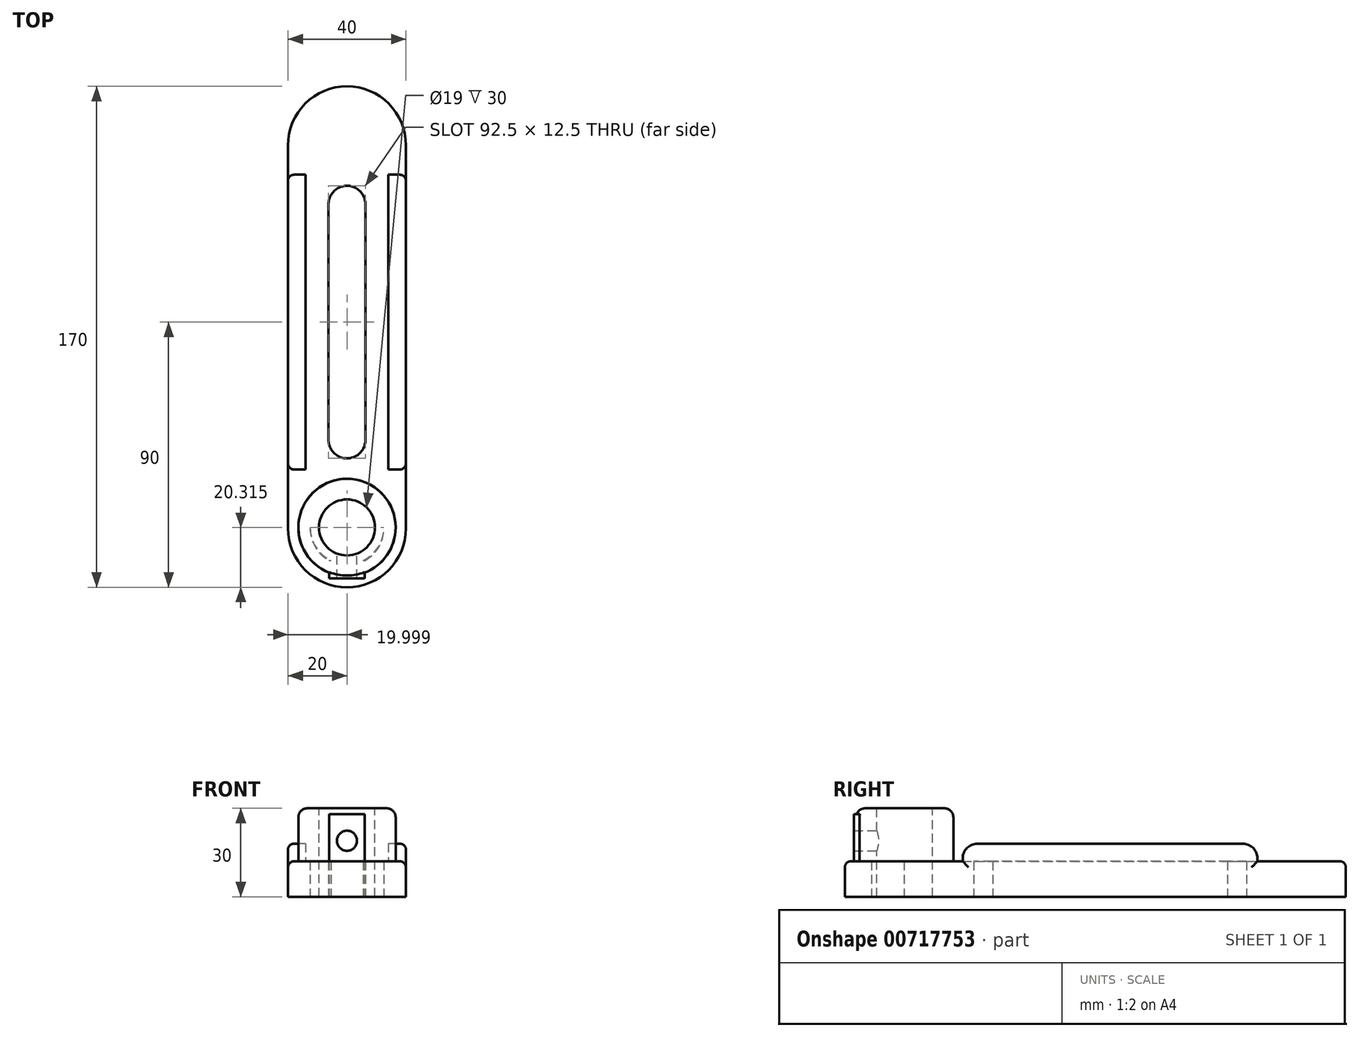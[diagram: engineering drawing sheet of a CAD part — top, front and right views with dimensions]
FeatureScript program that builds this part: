
annotation { "Feature Type Name" : "Feature", "Feature Type Description" : "" }
export const myFeature = defineFeature(function(context is Context, id is Id, definition is map)
    precondition{}
    {
        {
            var Q0;
            Q0=qCreatedBy(makeId("Top.planeOp"),FACE);
            var sketch = newSketch(context, id + "F0", { "sketchPlane" : qUnion([Q0])});
            skLineSegment(sketch, "E0.top", {"start": v(20, 80) * mm, "end": v(-20, 80) * mm});
            skLineSegment(sketch, "E0.left", {"start": v(20, -70) * mm, "end": v(20, 80) * mm});
            skLineSegment(sketch, "E0.right", {"start": v(-20, -70) * mm, "end": v(-20, 80) * mm});
            skPoint(sketch, "E0.middle", {"position": v(0, 0) * mm});
            skLineSegment(sketch, "E1", {"start": v(0, 0) * mm, "end": v(0, 40) * mm, "construction": true});
            skLineSegment(sketch, "E2", {"start": v(0, 40) * mm, "end": v(0, -40) * mm, "construction": true});
            skArc(sketch, "E3", {"start": v(-6.25, -40) * mm, "mid": v(0.07, -46.25) * mm, "end": v(6.25, -39.85) * mm});
            skArc(sketch, "E4", {"start": v(6.25, 39.85) * mm, "mid": v(0.07, 46.25) * mm, "end": v(-6.25, 40) * mm});
            skLineSegment(sketch, "E5", {"start": v(-6.25, 40) * mm, "end": v(-6.25, -40) * mm});
            skLineSegment(sketch, "E6", {"start": v(6.25, 40.15) * mm, "end": v(6.25, -40.15) * mm});
            skLineSegment(sketch, "E7", {"start": v(0, -90) * mm, "end": v(0, -70) * mm, "construction": true});
            skLineSegment(sketch, "E8", {"start": v(0, -70) * mm, "end": v(62.72, -70) * mm, "construction": true});
            skCircle(sketch, "E9", {"center": v(0, -70) * mm, "radius": 12.5 * mm});
            skArc(sketch, "E10", {"start": v(-20, -70) * mm, "mid": v(0, -90) * mm, "end": v(20, -70) * mm});
            skSolve(sketch);
        }
        {
            var Q0;
            Q0=makeQuery(id+"F0.imprint","IMPRINT",FACE,{"disambiguationData":[TD([[makeQuery(id+"F0.imprint","IMPRINT",EDGE,{"derivedFrom":sQuery(id+"F0.wireOp",EDGE,"E0.top")}),1.0]])]});
            extrude(context, id + "F1", {"entities" : qUnion([Q0]), "depth" : 12 * mm});
        }
        {
            var Q0;
            Q0=qCreatedBy(makeId("Top.planeOp"),FACE);
            var sketch = newSketch(context, id + "F2", { "sketchPlane" : qUnion([Q0])});
            skCircle(sketch, "E11", {"center": v(0, -69.69) * mm, "radius": 12.5 * mm});
            skCircle(sketch, "E12", {"center": v(0, -69.69) * mm, "radius": 16.5 * mm});
            skCircle(sketch, "E13", {"center": v(0, -69.69) * mm, "radius": 9.5 * mm});
            skSolve(sketch);
        }
        {
            var Q0;
            Q0=makeQuery(id+"F2.imprint","IMPRINT",FACE,{"disambiguationData":[TD([[makeQuery(id+"F2.imprint","IMPRINT",EDGE,{"derivedFrom":sQuery(id+"F2.wireOp",EDGE,"E11")}),-1.0]])]});
            var Q1;
            Q1=makeQuery(id+"F2.imprint","IMPRINT",FACE,{"disambiguationData":[TD([[makeQuery(id+"F2.imprint","IMPRINT",EDGE,{"derivedFrom":sQuery(id+"F2.wireOp",EDGE,"E11")}),1.0]])]});
            extrude(context, id + "F3", {"entities" : qUnion([Q0, Q1]), "operationType" : NewBodyOperationType.ADD, "depth" : 30 * mm, "hasSecondDirection" : true, "secondDirectionOppositeDirection" : false, "secondDirectionDepth" : 12 * mm});
        }
        {
            var Q0;
            Q0=makeQuery(id+"F2.imprint","IMPRINT",FACE,{"disambiguationData":[TD([[makeQuery(id+"F2.imprint","IMPRINT",EDGE,{"derivedFrom":sQuery(id+"F2.wireOp",EDGE,"E13")}),1.0]])]});
            var Q1;
            Q1=makeQuery(id+"F2.imprint","IMPRINT",FACE,{"disambiguationData":[TD([[makeQuery(id+"F2.imprint","IMPRINT",EDGE,{"derivedFrom":sQuery(id+"F2.wireOp",EDGE,"E11")}),1.0]])]});
            extrude(context, id + "F4", {"entities" : qUnion([Q0, Q1]), "operationType" : NewBodyOperationType.ADD, "depth" : 30 * mm});
        }
        {
            var Q0;
            Q0=qCreatedBy(makeId("Top.planeOp"),FACE);
            var sketch = newSketch(context, id + "F5", { "sketchPlane" : qUnion([Q0])});
            skCircle(sketch, "E14", {"center": v(0, -69.69) * mm, "radius": 9.5 * mm});
            skSolve(sketch);
        }
        {
            var Q0;
            Q0=qSketchRegion(id+"F5",true);
            extrude(context, id + "F6", {"entities" : qUnion([Q0]), "operationType" : NewBodyOperationType.REMOVE, "oppositeDirection" : true, "depth" : 25 * mm, "hasSecondDirection" : true, "secondDirectionOppositeDirection" : false, "secondDirectionDepth" : 100 * mm});
        }
        {
            var Q0;
            Q0=makeQuery(id+"F3.opExtrude","CAP_EDGE",EDGE,{"disambiguationData":[OSD([sQuery(id+"F2.wireOp",EDGE,"E12")])],"isStart":false});
            var Q1;
            Q1=makeQuery(id+"F3.opExtrude","CAP_EDGE",EDGE,{"disambiguationData":[OSD([sQuery(id+"F2.wireOp",EDGE,"E12")])],"isStart":true});
            fillet(context, id + "F7", {"entities" : qUnion([Q0, Q1]), "radius" : 3 * mm, "tangentPropagation" : true, "allowEdgeOverflow" : false});
        }
        {
            var Q0;
            Q0=qCreatedBy(makeId("Front.planeOp"),FACE);
            var sketch = newSketch(context, id + "F8", { "sketchPlane" : qUnion([Q0])});
            skLineSegment(sketch, "E15", {"start": v(14, 0) * mm, "end": v(20, 0) * mm, "construction": true});
            skLineSegment(sketch, "E16", {"start": v(20, 0) * mm, "end": v(20, 18) * mm});
            skLineSegment(sketch, "E17", {"start": v(20, 18) * mm, "end": v(14, 18) * mm});
            skLineSegment(sketch, "E18", {"start": v(14, 18) * mm, "end": v(14, 12) * mm});
            skLineSegment(sketch, "E19", {"start": v(-14, 12) * mm, "end": v(-14, 18) * mm});
            skLineSegment(sketch, "E20", {"start": v(-14, 18) * mm, "end": v(-20, 18) * mm});
            skLineSegment(sketch, "E21", {"start": v(-20, 18) * mm, "end": v(-20, 0) * mm});
            skLineSegment(sketch, "E22", {"start": v(-20, 0) * mm, "end": v(-14, 0) * mm});
            skLineSegment(sketch, "E23", {"start": v(-14, 12) * mm, "end": v(-14, 0) * mm});
            skLineSegment(sketch, "E24", {"start": v(14, 12) * mm, "end": v(14, 0) * mm});
            skLineSegment(sketch, "E25.trimOffspring", {"start": v(0, 0) * mm, "end": v(20, 0) * mm});
            skSolve(sketch);
        }
        {
            var Q0;
            Q0=qSketchRegion(id+"F8",true);
            extrude(context, id + "F9", {"entities" : qUnion([Q0]), "operationType" : NewBodyOperationType.ADD, "depth" : 50 * mm, "hasSecondDirection" : true, "secondDirectionOppositeDirection" : true, "secondDirectionDepth" : 50 * mm});
        }
        {
            var Q0;
            Q0=makeQuery(id+"F9.opExtrude","CAP_EDGE",EDGE,{"disambiguationData":[OSD([sQuery(id+"F8.wireOp",EDGE,"E17")])],"isStart":true});
            var Q1;
            Q1=makeQuery(id+"F9.opExtrude","CAP_EDGE",EDGE,{"disambiguationData":[OSD([sQuery(id+"F8.wireOp",EDGE,"E20")])],"isStart":true});
            var Q2;
            Q2=makeQuery(id+"F9.opExtrude","CAP_EDGE",EDGE,{"disambiguationData":[OSD([sQuery(id+"F8.wireOp",EDGE,"E20")])],"isStart":false});
            var Q3;
            Q3=makeQuery(id+"F9.opExtrude","CAP_EDGE",EDGE,{"disambiguationData":[OSD([sQuery(id+"F8.wireOp",EDGE,"E17")])],"isStart":false});
            fillet(context, id + "F10", {"entities" : qUnion([Q0, Q1, Q2, Q3]), "radius" : 5 * mm, "tangentPropagation" : true, "allowEdgeOverflow" : false});
        }
        {
            var Q0;
            Q0=makeQuery(id+"F1.opExtrude","SWEPT_EDGE",EDGE,{"disambiguationData":[OSD([sQuery(id+"F0.wireOp",EDGE,"E0.top"),sQuery(id+"F0.wireOp",EDGE,"E0.right")])]});
            var Q1;
            Q1=makeQuery(id+"F1.opExtrude","SWEPT_EDGE",EDGE,{"disambiguationData":[OSD([sQuery(id+"F0.wireOp",EDGE,"E0.top"),sQuery(id+"F0.wireOp",EDGE,"E0.left")])]});
            fillet(context, id + "F11", {"entities" : qUnion([Q0, Q1]), "radius" : 20 * mm, "tangentPropagation" : true, "allowEdgeOverflow" : false});
        }
        {
            var Q0;
            Q0=qCreatedBy(makeId("Top.planeOp"),FACE);
            var sketch = newSketch(context, id + "F12", { "sketchPlane" : qUnion([Q0])});
            skLineSegment(sketch, "E26.bottom", {"start": v(6, -86.93) * mm, "end": v(-6, -86.93) * mm});
            skLineSegment(sketch, "E26.top", {"start": v(6, -80.93) * mm, "end": v(-6, -80.93) * mm});
            skLineSegment(sketch, "E26.left", {"start": v(6, -86.93) * mm, "end": v(6, -80.93) * mm});
            skLineSegment(sketch, "E26.right", {"start": v(-6, -86.93) * mm, "end": v(-6, -80.93) * mm});
            skPoint(sketch, "E26.middle", {"position": v(0, -83.93) * mm});
            skSolve(sketch);
        }
        {
            var Q0;
            Q0=qSketchRegion(id+"F12",true);
            extrude(context, id + "F13", {"entities" : qUnion([Q0]), "operationType" : NewBodyOperationType.ADD, "depth" : 28 * mm});
        }
        {
            var Q0;
            Q0=qCreatedBy(makeId("Front.planeOp"),FACE);
            var sketch = newSketch(context, id + "F14", { "sketchPlane" : qUnion([Q0])});
            skLineSegment(sketch, "E27", {"start": v(0, 0) * mm, "end": v(0, 19) * mm, "construction": true});
            skLineSegment(sketch, "E28", {"start": v(0, 19) * mm, "end": v(-52.5, 19) * mm, "construction": true});
            skCircle(sketch, "E29", {"center": v(0, 19) * mm, "radius": 3.4 * mm});
            skSolve(sketch);
        }
        {
            var Q0;
            Q0=qSketchRegion(id+"F14",true);
            extrude(context, id + "F15", {"entities" : qUnion([Q0]), "operationType" : NewBodyOperationType.REMOVE, "depth" : 100 * mm, "hasSecondDirection" : true, "secondDirectionOppositeDirection" : false, "secondDirectionDepth" : 70 * mm});
        }
        {
            var Q0;
            {var subQ1=sQuery(id+"F0.wireOp",EDGE,"E0.left");var subQ2=sQuery(id+"F0.wireOp",EDGE,"E0.top");Q0=makeQuery(id+"F9.boolean.opBoolean","SPLIT",EDGE,{"disambiguationData":[TD([makeQuery(id+"F1.opExtrude","SWEPT_FACE",FACE,{"disambiguationData":[OSD([subQ2])]})])],"derivedFrom":makeQuery(id+"F1.opExtrude","CAP_EDGE",EDGE,{"disambiguationData":[OSD([subQ1])],"isStart":false})});}
            var Q1;
            {var subQ0=sQuery(id+"F0.wireOp",EDGE,"E0.right");var subQ1=sQuery(id+"F0.wireOp",EDGE,"E0.top");Q1=makeQuery(id+"F11.opFillet","BLEND_EDGE",EDGE,{"blendedFrom":[makeQuery(id+"F1.opExtrude","SWEPT_EDGE",EDGE,{"disambiguationData":[OSD([subQ1,subQ0])]}),makeQuery(id+"F1.opExtrude","CAP_FACE",FACE,{"disambiguationData":[OSD([subQ1,sQuery(id+"F0.wireOp",EDGE,"E0.left"),subQ0,sQuery(id+"F0.wireOp",EDGE,"E3"),sQuery(id+"F0.wireOp",EDGE,"E4"),sQuery(id+"F0.wireOp",EDGE,"E5"),sQuery(id+"F0.wireOp",EDGE,"E6"),sQuery(id+"F0.wireOp",EDGE,"E9"),sQuery(id+"F0.wireOp",EDGE,"E10")])],"isStart":false})],"blendedInto":[makeQuery(id+"F1.opExtrude","CAP_FACE",FACE,{"disambiguationData":[OSD([subQ1,sQuery(id+"F0.wireOp",EDGE,"E0.left"),subQ0,sQuery(id+"F0.wireOp",EDGE,"E3"),sQuery(id+"F0.wireOp",EDGE,"E4"),sQuery(id+"F0.wireOp",EDGE,"E5"),sQuery(id+"F0.wireOp",EDGE,"E6"),sQuery(id+"F0.wireOp",EDGE,"E9"),sQuery(id+"F0.wireOp",EDGE,"E10")])],"isStart":false})]});}
            var Q2;
            {var subQ1=sQuery(id+"F0.wireOp",EDGE,"E0.right");var subQ2=sQuery(id+"F0.wireOp",EDGE,"E0.top");Q2=makeQuery(id+"F9.boolean.opBoolean","SPLIT",EDGE,{"disambiguationData":[TD([makeQuery(id+"F1.opExtrude","SWEPT_FACE",FACE,{"disambiguationData":[OSD([subQ2])]})])],"derivedFrom":makeQuery(id+"F1.opExtrude","CAP_EDGE",EDGE,{"disambiguationData":[OSD([subQ1])],"isStart":false})});}
            var Q3;
            {var subQ1=sQuery(id+"F0.wireOp",EDGE,"E10");var subQ2=sQuery(id+"F0.wireOp",EDGE,"E0.left");Q3=makeQuery(id+"F9.boolean.opBoolean","SPLIT",EDGE,{"disambiguationData":[TD([makeQuery(id+"F1.opExtrude","SWEPT_FACE",FACE,{"disambiguationData":[OSD([subQ1])]})])],"derivedFrom":makeQuery(id+"F1.opExtrude","CAP_EDGE",EDGE,{"disambiguationData":[OSD([subQ2])],"isStart":false})});}
            var Q4;
            Q4=makeQuery(id+"F10.opFillet","BLEND_EDGE",EDGE,{"blendedFrom":[makeQuery(id+"F9.opExtrude","CAP_EDGE",EDGE,{"disambiguationData":[OSD([sQuery(id+"F8.wireOp",EDGE,"E20")])],"isStart":false}),makeQuery(id+"F9.boolean.opBoolean","MERGE",FACE,{"derivedFrom":[makeQuery(id+"F1.opExtrude","SWEPT_FACE",FACE,{"disambiguationData":[OSD([sQuery(id+"F0.wireOp",EDGE,"E0.right")])]}),makeQuery(id+"F9.opExtrude","SWEPT_FACE",FACE,{"disambiguationData":[OSD([sQuery(id+"F8.wireOp",EDGE,"E21")])]})]})],"blendedInto":[makeQuery(id+"F9.boolean.opBoolean","MERGE",FACE,{"derivedFrom":[makeQuery(id+"F1.opExtrude","SWEPT_FACE",FACE,{"disambiguationData":[OSD([sQuery(id+"F0.wireOp",EDGE,"E0.right")])]}),makeQuery(id+"F9.opExtrude","SWEPT_FACE",FACE,{"disambiguationData":[OSD([sQuery(id+"F8.wireOp",EDGE,"E21")])]})]})]});
            var Q5;
            Q5=makeQuery(id+"F9.opExtrude","SWEPT_EDGE",EDGE,{"disambiguationData":[OSD([sQuery(id+"F8.wireOp",EDGE,"E20"),sQuery(id+"F8.wireOp",EDGE,"E21")])]});
            var Q6;
            Q6=makeQuery(id+"F9.opExtrude","SWEPT_EDGE",EDGE,{"disambiguationData":[OSD([sQuery(id+"F8.wireOp",EDGE,"E16"),sQuery(id+"F8.wireOp",EDGE,"E17")])]});
            var Q7;
            Q7=makeQuery(id+"F10.opFillet","BLEND_EDGE",EDGE,{"blendedFrom":[makeQuery(id+"F9.opExtrude","CAP_EDGE",EDGE,{"disambiguationData":[OSD([sQuery(id+"F8.wireOp",EDGE,"E17")])],"isStart":false}),makeQuery(id+"F9.boolean.opBoolean","MERGE",FACE,{"derivedFrom":[makeQuery(id+"F1.opExtrude","SWEPT_FACE",FACE,{"disambiguationData":[OSD([sQuery(id+"F0.wireOp",EDGE,"E0.left")])]}),makeQuery(id+"F9.opExtrude","SWEPT_FACE",FACE,{"disambiguationData":[OSD([sQuery(id+"F8.wireOp",EDGE,"E16")])]})]})],"blendedInto":[makeQuery(id+"F9.boolean.opBoolean","MERGE",FACE,{"derivedFrom":[makeQuery(id+"F1.opExtrude","SWEPT_FACE",FACE,{"disambiguationData":[OSD([sQuery(id+"F0.wireOp",EDGE,"E0.left")])]}),makeQuery(id+"F9.opExtrude","SWEPT_FACE",FACE,{"disambiguationData":[OSD([sQuery(id+"F8.wireOp",EDGE,"E16")])]})]})]});
            fillet(context, id + "F16", {"entities" : qUnion([Q0, Q1, Q2, Q3, Q4, Q5, Q6, Q7]), "radius" : 2 * mm, "tangentPropagation" : true, "allowEdgeOverflow" : false});
        }
    });
